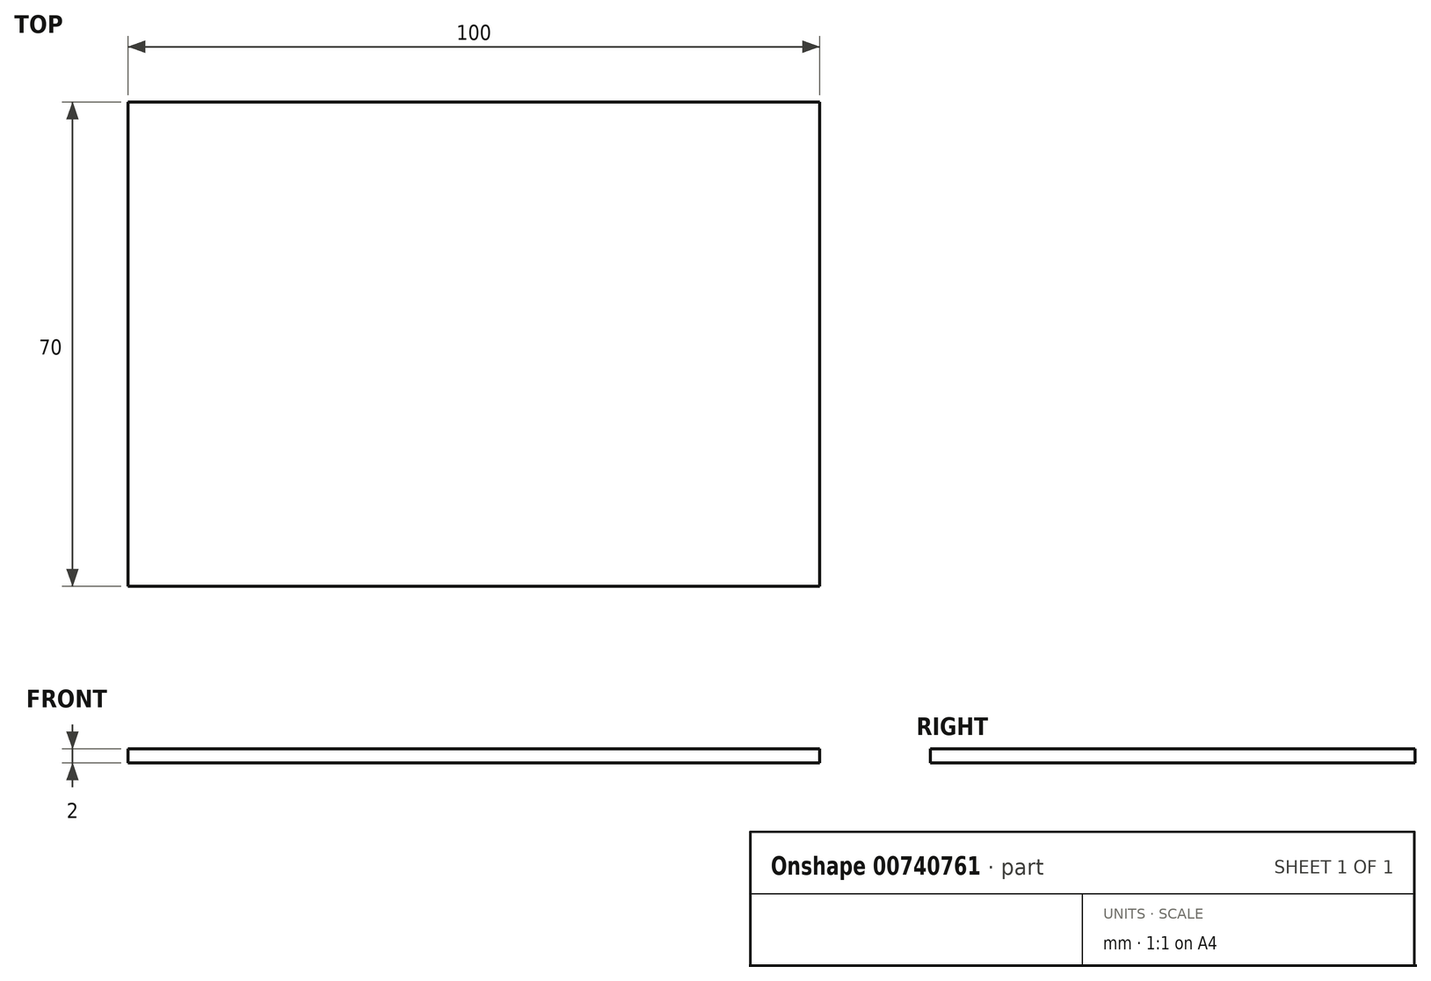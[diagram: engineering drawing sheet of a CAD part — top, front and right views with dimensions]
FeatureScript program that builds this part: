
annotation { "Feature Type Name" : "Feature", "Feature Type Description" : "" }
export const myFeature = defineFeature(function(context is Context, id is Id, definition is map)
    precondition{}
    {
        {
            var Q0;
            Q0=qCreatedBy(makeId("Top.planeOp"),FACE);
            var sketch = newSketch(context, id + "F0", { "sketchPlane" : qUnion([Q0])});
            skLineSegment(sketch, "E0.bottom", {"start": v(-50, 35) * mm, "end": v(50, 35) * mm});
            skLineSegment(sketch, "E0.top", {"start": v(-50, -35) * mm, "end": v(50, -35) * mm});
            skLineSegment(sketch, "E0.left", {"start": v(-50, 35) * mm, "end": v(-50, -35) * mm});
            skLineSegment(sketch, "E0.right", {"start": v(50, 35) * mm, "end": v(50, -35) * mm});
            skPoint(sketch, "E0.middle", {"position": v(0, 0) * mm});
            skSolve(sketch);
        }
        {
            var Q0;
            Q0=makeQuery(id+"F0.imprint","IMPRINT",FACE,{"disambiguationData":[TD([[makeQuery(id+"F0.imprint","IMPRINT",EDGE,{"derivedFrom":sQuery(id+"F0.wireOp",EDGE,"E0.bottom")}),-1.0]])]});
            extrude(context, id + "F1", {"entities" : qUnion([Q0]), "depth" : 2 * mm, "offsetDistance" : 25 * mm});
        }
    });
